FREECAD ASSEMBLY — COMPONENT RECIPES ("tinyMakeShelves")

This assembly document has 16 components, labeled P0..P15 below (a component is one placed body or linked part). 16 of them carry a construction recipe — the FreeCAD feature program that regenerates the part from scratch, quoted from this document or its linked companion documents; the rest are supplied as boundary geometry only. No exploded tour is included for this assembly.
COMPONENT P0 — recipe-attached ("expectations-Part", a linked part whose construction recipe lives in a companion FreeCAD document of the same project; that document's serialized recipe follows).
Construction recipe (the companion document, serialized — sketch geometry with constraints, then the solid features built on it; lengths are millimeters unless a unit is written):

FCSTD DOCUMENT  (FreeCAD 2023.131R26244 +5365 (Git))
Label: expectations
License: All rights reserved
LicenseURL: http://en.wikipedia.org/wiki/All_rights_reserved
objects: Sketcher::SketchObject×3, PartDesign::Pad×3, PartDesign::Body×1, App::Part×1
note: 16 computed .brp shape members not serialized (recipe doc carries the construction recipe); baked Part::Feature solids carry a one-line shape summary decoded from their .brp

FEATURE [Sketcher::SketchObject] Sketch
  ArcFitTolerance = 1e-06
  ExternalBSplineMaxDegree = 5
  ExternalBSplineTolerance = 0.0001
  FixShape = 1
  FullyConstrained = true
  InternalTolerance = 1e-06
  InvalidShape = false
  MakeInternals = false
  MapMode = 2
  TreeRank = 5
  ValidateShape = false
  sketch-geometry (6):
    g0: LineSegment StartX=0 StartY=0 StartZ=0 EndX=0 EndY=2235.2 EndZ=0
    g1: LineSegment StartX=0 StartY=2235.2 StartZ=0 EndX=685.8 EndY=2921 EndZ=0
    g2: LineSegment StartX=685.8 StartY=2921 StartZ=0 EndX=3606.8 EndY=2921 EndZ=0
    g3: LineSegment StartX=3606.8 StartY=2921 StartZ=0 EndX=4013.2 EndY=2514.6 EndZ=0
    g4: LineSegment StartX=4013.2 StartY=2514.6 StartZ=0 EndX=4013.2 EndY=0 EndZ=0
    g5: LineSegment StartX=4013.2 StartY=0 StartZ=0 EndX=0 EndY=0 EndZ=0
  constraints (17):
    c: Coincident(g0,g-1)
    c: Vertical(g0)
    c: Coincident(g1,g0)
    c: Coincident(g2,g1)
    c: Horizontal(g2)
    c: Coincident(g3,g2)
    c: Coincident(g4,g3)
    c: PointOnObject(g4,g-1)
    c: Vertical(g4)
    c: Coincident(g5,g4)
    c: Coincident(g5,g0)
    c: DistanceY(g0,g1) = 2921
    c: DistanceX(g5,g5) = 4013.2
    c: DistanceY(g0,g0) = 2235.2
    c: DistanceY(g4,g3) = 2514.6
    c: Angle(g0,g1) = 2.35619
    c: Angle(g3,g4) = 2.35619
FEATURE [PartDesign::Pad] Pad
  AddSubType = 0
  AlongSketchNormal = false
  AutoTaperInnerAngle = true
  CheckUpToFaceLimits = true
  ClaimChildren = false
  Direction = (0,0,1)
  Fit = 0
  FitJoin = 0
  FixShape = 1
  InnerFit = 0
  InnerFitJoin = 0
  InvalidShape = false
  Length = 10
  Length2 = 100
  Linearize = true
  NewSolid = false
  Profile = -> Sketch
  Reversed = true
  Suppress = false
  TaperInnerAngle = 0
  TaperInnerAngleRev = 0
  TreeRank = 16
  Type = 0
  ValidateShape = false
  _ProfileBasedVersion = 1
FEATURE [Sketcher::SketchObject] Sketch001
  ArcFitTolerance = 1e-06
  AttachmentSupport = -> [XZ_Plane]
  ExternalBSplineMaxDegree = 5
  ExternalBSplineTolerance = 0.0001
  ExternalGeometry = -> [Pad]
  FixShape = 1
  FullyConstrained = true
  InternalTolerance = 1e-06
  InvalidShape = false
  MakeInternals = false
  MapMode = 5
  Placement = pos=(0,0,0) rot=(1,0,0;1.5708rad)
  Support = -> [XZ_Plane]
  TreeRank = 17
  ValidateShape = false
  sketch-geometry (4):
    g0: LineSegment StartX=0 StartY=0 StartZ=0 EndX=4013.2 EndY=0 EndZ=0
    g1: LineSegment StartX=4013.2 StartY=0 StartZ=0 EndX=4013.2 EndY=3556 EndZ=0
    g2: LineSegment StartX=4013.2 StartY=3556 StartZ=0 EndX=0 EndY=3556 EndZ=0
    g3: LineSegment StartX=0 StartY=3556 StartZ=0 EndX=0 EndY=0 EndZ=0
  constraints (11):
    c: Coincident(g0,g1)
    c: Coincident(g1,g2)
    c: Coincident(g2,g3)
    c: Coincident(g3,g0)
    c: Horizontal(g0)
    c: Horizontal(g2)
    c: Vertical(g1)
    c: Vertical(g3)
    c: Coincident(g0,g-1)
    c: PointOnObject(g-3,g1)
    c: DistanceY(g3,g3) = 3556
FEATURE [PartDesign::Pad] Pad001
  AddSubType = 0
  AlongSketchNormal = false
  AutoTaperInnerAngle = true
  BaseFeature = -> Pad
  CheckUpToFaceLimits = true
  ClaimChildren = false
  Direction = (0,-1,-2e-16)
  Fit = 0
  FitJoin = 0
  FixShape = 1
  InnerFit = 0
  InnerFitJoin = 0
  InvalidShape = false
  Length = 10
  Length2 = 100
  Linearize = true
  NewSolid = false
  Profile = -> Sketch001
  Reversed = true
  Suppress = false
  TaperInnerAngle = 0
  TaperInnerAngleRev = 0
  TreeRank = 18
  Type = 0
  ValidateShape = false
  _ProfileBasedVersion = 1
FEATURE [Sketcher::SketchObject] Sketch002
  ArcFitTolerance = 1e-06
  AttachmentSupport = -> [Pad001]
  ExternalBSplineMaxDegree = 5
  ExternalBSplineTolerance = 0.0001
  FixShape = 1
  FullyConstrained = true
  InternalTolerance = 1e-06
  InvalidShape = false
  MakeInternals = false
  MapMode = 5
  Placement = pos=(4013.2,0,0) rot=(0.57735,0.57735,0.57735;2.0944rad)
  Support = -> [Pad001]
  TreeRank = 19
  ValidateShape = false
  sketch-geometry (5):
    g0: LineSegment StartX=0 StartY=1422.4 StartZ=0 EndX=2057.4 EndY=1422.4 EndZ=0
    g1: LineSegment StartX=2057.4 StartY=1422.4 StartZ=0 EndX=2057.4 EndY=3289.3 EndZ=0
    g2: LineSegment StartX=2057.4 StartY=3289.3 StartZ=0 EndX=0 EndY=3289.3 EndZ=0
    g3: LineSegment StartX=0 StartY=3289.3 StartZ=0 EndX=0 EndY=1422.4 EndZ=0
    g4: LineSegment [constr] StartX=0 StartY=-1.8e-15 StartZ=0 EndX=0 EndY=1422.4 EndZ=0
  constraints (14):
    c: Coincident(g0,g1)
    c: Coincident(g1,g2)
    c: Coincident(g2,g3)
    c: Coincident(g3,g0)
    c: Horizontal(g0)
    c: Horizontal(g2)
    c: Vertical(g1)
    c: Vertical(g3)
    c: Coincident(g4,g-1)
    c: Coincident(g4,g0)
    c: DistanceY(g4,g4) = 1422.4
    c: DistanceY(g3,g3) = 1866.9
    c: DistanceX(g0,g0) = 2057.4
    c: Vertical(g4)
FEATURE [PartDesign::Pad] Pad002
  AddSubType = 0
  AlongSketchNormal = false
  AutoTaperInnerAngle = true
  BaseFeature = -> Pad001
  CheckUpToFaceLimits = true
  ClaimChildren = false
  Direction = (1,0,0)
  Fit = 0
  FitJoin = 0
  FixShape = 1
  InnerFit = 0
  InnerFitJoin = 0
  InvalidShape = false
  Length = 10
  Length2 = 100
  Linearize = true
  NewSolid = false
  Profile = -> Sketch002
  Suppress = false
  TaperInnerAngle = 0
  TaperInnerAngleRev = 0
  TreeRank = 20
  Type = 0
  ValidateShape = false
  _ProfileBasedVersion = 1
FEATURE [PartDesign::Body] Body
  AutoGroupSolids = false
  ClaimAllChildren = false
  ExportMode = 0
  FixShape = 1
  Group = -> [Sketch,Pad,Sketch001,Pad001,Sketch002,Pad002]
  InvalidShape = false
  Origin = -> Origin001
  Tip = -> Pad002
  TreeRank = 15
  ValidateShape = false
  _ExportChildren = -> [Pad,Pad001,Pad002]
  _GroupVersion = 1
FEATURE [App::Part] Part  label="expectations-Part"
  ClaimAllChildren = false
  ExportMode = 1
  Group = -> [Body]
  Origin = -> Origin
  TreeRank = 4
  _ExportChildren = -> [Body]
  _GroupVersion = 1
COMPONENT P1 — recipe-attached ("Workstation-SevilleClassics_AirliftProS3-Part", a linked part whose construction recipe lives in a companion FreeCAD document of the same project; that document's serialized recipe follows).
Construction recipe (the companion document, serialized — sketch geometry with constraints, then the solid features built on it; lengths are millimeters unless a unit is written):

FCSTD DOCUMENT  (FreeCAD 2023.131R26244 +5365 (Git))
Label: Workstation-SevilleClassics_AirliftProS3
License: All rights reserved
LicenseURL: http://en.wikipedia.org/wiki/All_rights_reserved
objects: PartDesign::Pad×4, Sketcher::SketchObject×2, PartDesign::Body×1, App::Part×1
note: 17 computed .brp shape members not serialized (recipe doc carries the construction recipe); baked Part::Feature solids carry a one-line shape summary decoded from their .brp

FEATURE [Sketcher::SketchObject] Sketch
  ArcFitTolerance = 1e-06
  AttachmentSupport = -> [XY_Plane]
  ExternalBSplineMaxDegree = 5
  ExternalBSplineTolerance = 0.0001
  FixShape = 1
  FullyConstrained = true
  InternalTolerance = 1e-06
  InvalidShape = false
  MakeInternals = false
  MapMode = 5
  Support = -> [XY_Plane]
  TreeRank = 13
  ValidateShape = false
  sketch-geometry (4):
    g0: LineSegment StartX=-1479.55 StartY=0 StartZ=0 EndX=1479.55 EndY=0 EndZ=0
    g1: LineSegment StartX=1479.55 StartY=0 StartZ=0 EndX=1479.55 EndY=762 EndZ=0
    g2: LineSegment StartX=1479.55 StartY=762 StartZ=0 EndX=-1479.55 EndY=762 EndZ=0
    g3: LineSegment StartX=-1479.55 StartY=762 StartZ=0 EndX=-1479.55 EndY=0 EndZ=0
  constraints (11):
    c: Coincident(g0,g1)
    c: Coincident(g1,g2)
    c: Coincident(g2,g3)
    c: Coincident(g3,g0)
    c: Horizontal(g0)
    c: Horizontal(g2)
    c: Vertical(g1)
    c: Vertical(g3)
    c: Symmetric(g0,g0,g-1)
    c: DistanceY(g3,g3) = 762
    c: DistanceX(g0,g0) = 2959.1
FEATURE [PartDesign::Pad] Pad
  AddSubType = 0
  AlongSketchNormal = false
  AutoTaperInnerAngle = true
  CheckUpToFaceLimits = true
  ClaimChildren = false
  Direction = (0,0,1)
  Fit = 0
  FitJoin = 0
  FixShape = 1
  InnerFit = 0
  InnerFitJoin = 0
  InvalidShape = false
  Length = 76.2
  Length2 = 100
  Linearize = true
  NewSolid = false
  Profile = -> Sketch
  Reversed = true
  Suppress = false
  TaperInnerAngle = 0
  TaperInnerAngleRev = 0
  TreeRank = 14
  Type = 0
  ValidateShape = false
  _ProfileBasedVersion = 1
FEATURE [PartDesign::Pad] Pad001
  AddSubType = 0
  AlongSketchNormal = false
  AutoTaperInnerAngle = true
  CheckUpToFaceLimits = true
  ClaimChildren = false
  Direction = (0,0,1)
  Fit = 0
  FitJoin = 0
  FixShape = 1
  InnerFit = 0
  InnerFitJoin = 0
  InvalidShape = false
  Length = 965.2
  Length2 = -76.2
  Linearize = true
  NewSolid = true
  Profile = -> Sketch
  Reversed = true
  Suppress = false
  TaperInnerAngle = 0
  TaperInnerAngleRev = 0
  TreeRank = 15
  Type = 4
  ValidateShape = false
  _ProfileBasedVersion = 1
FEATURE [Sketcher::SketchObject] Sketch001
  ArcFitTolerance = 1e-06
  AttachmentSupport = -> [Sketch]
  ExternalBSplineMaxDegree = 5
  ExternalBSplineTolerance = 0.0001
  ExternalGeometry = -> [Sketch]
  FixShape = 1
  FullyConstrained = false
  InternalTolerance = 1e-06
  InvalidShape = false
  MakeInternals = false
  MapMode = 5
  Support = -> [Sketch]
  TreeRank = 16
  ValidateShape = false
  sketch-geometry (11):
    g0: LineSegment StartX=-723.9 StartY=609.6 StartZ=0 EndX=723.9 EndY=609.6 EndZ=0
    g1: LineSegment StartX=723.9 StartY=609.6 StartZ=0 EndX=1479.56 EndY=-347.179 EndZ=0
    g2: LineSegment StartX=-723.9 StartY=609.6 StartZ=0 EndX=-1479.56 EndY=-347.179 EndZ=0
    g3: LineSegment [constr] StartX=-1479.56 StartY=-347.179 StartZ=0 EndX=1479.56 EndY=-347.179 EndZ=0
    g4: GeomPoint [constr] X=1101.73 Y=131.21 Z=0
    g5: GeomPoint [constr] X=1205.36 Y=0 Z=0
    g6: LineSegment StartX=-1479.56 StartY=-347.179 StartZ=0 EndX=-1513.75 EndY=-347.179 EndZ=0
    g7: LineSegment StartX=-1513.75 StartY=-347.179 StartZ=0 EndX=-741.041 EndY=631.188 EndZ=0
    g8: LineSegment StartX=-741.041 StartY=631.188 StartZ=0 EndX=741.041 EndY=631.188 EndZ=0
    g9: LineSegment StartX=741.041 StartY=631.188 StartZ=0 EndX=1513.75 EndY=-347.179 EndZ=0
    g10: LineSegment StartX=1513.75 StartY=-347.179 StartZ=0 EndX=1479.56 EndY=-347.179 EndZ=0
  constraints (26):
    c: Symmetric(g0,g0,g-2)
    c: DistanceX(g0,g0) = 1447.8
    c: Coincident(g1,g0)
    c: Coincident(g2,g0)
    c: Coincident(g3,g2)
    c: Coincident(g3,g1)
    c: Symmetric(g1,g2,g-2)
    c: Distance(g1) = 1219.2
    c: DistanceY(g0,g-3) = 152.4
    c: Symmetric(g1,g1,g4)
    c: PointOnObject(g5,g1)
    c: PointOnObject(g5,g-1)
    c: Distance(g5,g4) = 167.198
    c: DistanceX(g2,g-3) = 0.01
    c: Coincident(g6,g2)
    c: PointOnObject(g6,g3)
    c: Coincident(g7,g6)
    c: Coincident(g8,g7)
    c: Horizontal(g8)
    c: Coincident(g9,g8)
    c: PointOnObject(g9,g3)
    c: Coincident(g10,g9)
    c: Coincident(g10,g1)
    c: Equal(g6,g10)
    c: Equal(g7,g9)
    c: Parallel(g9,g1)
FEATURE [PartDesign::Pad] Pad002
  AddSubType = 0
  AlongSketchNormal = false
  AutoTaperInnerAngle = true
  CheckUpToFaceLimits = true
  ClaimChildren = false
  Direction = (0,0,1)
  Fit = 0
  FitJoin = 0
  FixShape = 1
  InnerFit = 0
  InnerFitJoin = 0
  InvalidShape = false
  Length = 965.2
  Length2 = 100
  Linearize = true
  NewSolid = true
  Profile = -> Sketch001
  Suppress = false
  TaperInnerAngle = 0
  TaperInnerAngleRev = 0
  TreeRank = 17
  Type = 0
  ValidateShape = false
  _ProfileBasedVersion = 1
FEATURE [PartDesign::Pad] Pad003
  AddSubType = 0
  AlongSketchNormal = false
  AutoTaperInnerAngle = true
  CheckUpToFaceLimits = true
  ClaimChildren = false
  Direction = (0,0,1)
  Fit = 0
  FitJoin = 0
  FixShape = 1
  InnerFit = 0
  InnerFitJoin = 0
  InvalidShape = false
  Length = 609.6
  Length2 = -76.2
  Linearize = true
  NewSolid = true
  Profile = -> Sketch
  Reversed = true
  Suppress = false
  TaperInnerAngle = 0
  TaperInnerAngleRev = 0
  TreeRank = 18
  Type = 4
  ValidateShape = false
  _ProfileBasedVersion = 1
FEATURE [PartDesign::Body] Body
  AutoGroupSolids = false
  ClaimAllChildren = false
  ExportMode = 0
  FixShape = 1
  Group = -> [Sketch,Pad,Pad001,Sketch001,Pad002,Pad003]
  InvalidShape = false
  Origin = -> Origin001
  Tip = -> Pad003
  TreeRank = 12
  ValidateShape = false
  _ExportChildren = -> [Pad,Pad001,Pad002,Pad003]
  _GroupVersion = 1
FEATURE [App::Part] Part  label="Workstation-SevilleClassics_AirliftProS3-Part"
  ClaimAllChildren = false
  ExportMode = 1
  Group = -> [Body]
  Origin = -> Origin
  TreeRank = 1
  _ExportChildren = -> [Body]
  _GroupVersion = 1
COMPONENT P2 — recipe-attached ("roadLegalWidth-Body", a linked part whose construction recipe lives in a companion FreeCAD document of the same project; that document's serialized recipe follows).
Construction recipe (the companion document, serialized — sketch geometry with constraints, then the solid features built on it; lengths are millimeters unless a unit is written):

FCSTD DOCUMENT  (FreeCAD 2023.131R26244 +5365 (Git))
Label: roadLegalWidth
License: All rights reserved
LicenseURL: http://en.wikipedia.org/wiki/All_rights_reserved
objects: Sketcher::SketchObject×1, PartDesign::Pad×1, PartDesign::Body×1, App::Part×1
note: 6 computed .brp shape members not serialized (recipe doc carries the construction recipe); baked Part::Feature solids carry a one-line shape summary decoded from their .brp

FEATURE [Sketcher::SketchObject] Sketch
  ArcFitTolerance = 1e-06
  AttachmentSupport = -> [XY_Plane]
  ExternalBSplineMaxDegree = 5
  ExternalBSplineTolerance = 0.0001
  FullyConstrained = true
  InternalTolerance = 1e-06
  InvalidShape = false
  MakeInternals = false
  MapMode = 5
  Support = -> [XY_Plane]
  TreeRank = 10
  ValidateShape = true
  sketch-geometry (4):
    g0: LineSegment StartX=0 StartY=0 StartZ=0 EndX=2590.8 EndY=0 EndZ=0
    g1: LineSegment StartX=2590.8 StartY=0 StartZ=0 EndX=2590.8 EndY=12192 EndZ=0
    g2: LineSegment StartX=2590.8 StartY=12192 StartZ=0 EndX=0 EndY=12192 EndZ=0
    g3: LineSegment StartX=0 StartY=12192 StartZ=0 EndX=0 EndY=0 EndZ=0
  constraints (11):
    c: Coincident(g0,g1)
    c: Coincident(g1,g2)
    c: Coincident(g2,g3)
    c: Coincident(g3,g0)
    c: Horizontal(g0)
    c: Horizontal(g2)
    c: Vertical(g1)
    c: Vertical(g3)
    c: Coincident(g0,g-1)
    c: DistanceX(g0,g0) = 2590.8
    c: DistanceY(g3,g3) = 12192
FEATURE [PartDesign::Pad] Pad
  AddSubType = 0
  AlongSketchNormal = false
  AutoTaperInnerAngle = true
  CheckUpToFaceLimits = true
  ClaimChildren = false
  Direction = (0,0,1)
  Fit = 0
  FitJoin = 0
  FixShape = 1
  InnerFit = 0
  InnerFitJoin = 0
  InvalidShape = false
  Length = 10
  Length2 = 100
  Linearize = true
  NewSolid = false
  Profile = -> Sketch
  Reversed = true
  Suppress = false
  TaperInnerAngle = 0
  TaperInnerAngleRev = 0
  TreeRank = 11
  Type = 0
  ValidateShape = false
  _ProfileBasedVersion = 1
FEATURE [PartDesign::Body] Body  label="roadLegalWidth-Body"
  AutoGroupSolids = false
  ClaimAllChildren = false
  ExportMode = 0
  Group = -> [Sketch,Pad]
  InvalidShape = false
  Origin = -> Origin
  Tip = -> Pad
  TreeRank = 9
  ValidateShape = true
  _ExportChildren = -> [Pad]
  _GroupVersion = 1
FEATURE [App::Part] Part  label="roadLegalWidth-Part"
  ClaimAllChildren = false
  ExportMode = 1
  Group = -> [Body]
  Origin = -> Origin001
  TreeRank = 14
  _ExportChildren = -> [Body]
  _GroupVersion = 1
COMPONENT P3 — recipe-attached ("bedQueen-Part", a linked part whose construction recipe lives in a companion FreeCAD document of the same project; that document's serialized recipe follows).
Construction recipe (the companion document, serialized — sketch geometry with constraints, then the solid features built on it; lengths are millimeters unless a unit is written):

FCSTD DOCUMENT  (FreeCAD 2023.131R26244 +5365 (Git))
Label: bedQueen
License: All rights reserved
LicenseURL: http://en.wikipedia.org/wiki/All_rights_reserved
objects: PartDesign::Pad×2, Sketcher::SketchObject×1, PartDesign::Body×1, App::Part×1
note: 9 computed .brp shape members not serialized (recipe doc carries the construction recipe); baked Part::Feature solids carry a one-line shape summary decoded from their .brp

FEATURE [Sketcher::SketchObject] Sketch
  ArcFitTolerance = 1e-06
  AttachmentSupport = -> [XY_Plane]
  ExternalBSplineMaxDegree = 5
  ExternalBSplineTolerance = 0.0001
  FixShape = 1
  FullyConstrained = true
  InternalTolerance = 1e-06
  InvalidShape = false
  MakeInternals = false
  MapMode = 5
  Support = -> [XY_Plane]
  TreeRank = 10
  ValidateShape = false
  sketch-geometry (4):
    g0: LineSegment StartX=0 StartY=0 StartZ=0 EndX=1524 EndY=0 EndZ=0
    g1: LineSegment StartX=1524 StartY=0 StartZ=0 EndX=1524 EndY=2032 EndZ=0
    g2: LineSegment StartX=1524 StartY=2032 StartZ=0 EndX=0 EndY=2032 EndZ=0
    g3: LineSegment StartX=0 StartY=2032 StartZ=0 EndX=0 EndY=0 EndZ=0
  constraints (11):
    c: Coincident(g0,g1)
    c: Coincident(g1,g2)
    c: Coincident(g2,g3)
    c: Coincident(g3,g0)
    c: Horizontal(g0)
    c: Horizontal(g2)
    c: Vertical(g1)
    c: Vertical(g3)
    c: Coincident(g0,g-1)
    c: DistanceX(g0,g0) = 1524
    c: DistanceY(g3,g3) = 2032
FEATURE [PartDesign::Pad] Pad
  AddSubType = 0
  AlongSketchNormal = false
  AutoTaperInnerAngle = true
  CheckUpToFaceLimits = true
  ClaimChildren = false
  Direction = (0,0,1)
  Fit = 0
  FitJoin = 0
  FixShape = 1
  InnerFit = 0
  InnerFitJoin = 0
  InvalidShape = false
  Length = 215.9
  Length2 = 100
  Linearize = true
  NewSolid = false
  Profile = -> Sketch
  Reversed = true
  Suppress = false
  TaperInnerAngle = 0
  TaperInnerAngleRev = 0
  TreeRank = 11
  Type = 0
  ValidateShape = false
  _ProfileBasedVersion = 1
FEATURE [PartDesign::Pad] Pad001
  AddSubType = 0
  AlongSketchNormal = false
  AutoTaperInnerAngle = true
  CheckUpToFaceLimits = true
  ClaimChildren = false
  Direction = (0,0,1)
  Fit = 0
  FitJoin = 0
  FixShape = 1
  InnerFit = 0
  InnerFitJoin = 0
  InvalidShape = false
  Length = 812.8
  Length2 = 100
  Linearize = true
  NewSolid = true
  Profile = -> Sketch
  Suppress = false
  TaperInnerAngle = 0
  TaperInnerAngleRev = 0
  TreeRank = 12
  Type = 0
  ValidateShape = false
  _ProfileBasedVersion = 1
FEATURE [PartDesign::Body] Body  label="bedQueen-Body"
  AutoGroupSolids = false
  ClaimAllChildren = false
  ExportMode = 0
  FixShape = 1
  Group = -> [Sketch,Pad,Pad001]
  InvalidShape = false
  Origin = -> Origin
  Tip = -> Pad001
  TreeRank = 9
  ValidateShape = false
  _ExportChildren = -> [Pad,Pad001]
  _GroupVersion = 1
FEATURE [App::Part] Part  label="bedQueen-Part"
  ClaimAllChildren = false
  ExportMode = 1
  Group = -> [Body]
  Origin = -> Origin001
  TreeRank = 15
  _ExportChildren = -> [Body]
  _GroupVersion = 1
COMPONENT P4 — recipe-attached ("human-Part", a linked part whose construction recipe lives in a companion FreeCAD document of the same project; that document's serialized recipe follows).
Construction recipe (the companion document, serialized — sketch geometry with constraints, then the solid features built on it; lengths are millimeters unless a unit is written):

FCSTD DOCUMENT  (FreeCAD 2023.131R26244 +5365 (Git))
Label: human
License: All rights reserved
LicenseURL: http://en.wikipedia.org/wiki/All_rights_reserved
objects: Sketcher::SketchObject×1, PartDesign::Pad×1, PartDesign::Body×1, App::Part×1
note: 6 computed .brp shape members not serialized (recipe doc carries the construction recipe); baked Part::Feature solids carry a one-line shape summary decoded from their .brp

FEATURE [Sketcher::SketchObject] Sketch
  ArcFitTolerance = 1e-06
  AttachmentSupport = -> [XY_Plane]
  ExternalBSplineMaxDegree = 5
  ExternalBSplineTolerance = 0.0001
  FixShape = 1
  FullyConstrained = true
  InternalTolerance = 1e-06
  InvalidShape = false
  MakeInternals = false
  MapMode = 5
  Support = -> [XY_Plane]
  TreeRank = 13
  ValidateShape = false
  sketch-geometry (4):
    g0: LineSegment StartX=0 StartY=0 StartZ=0 EndX=609.6 EndY=0 EndZ=0
    g1: LineSegment StartX=609.6 StartY=0 StartZ=0 EndX=609.6 EndY=609.6 EndZ=0
    g2: LineSegment StartX=609.6 StartY=609.6 StartZ=0 EndX=0 EndY=609.6 EndZ=0
    g3: LineSegment StartX=0 StartY=609.6 StartZ=0 EndX=0 EndY=0 EndZ=0
  constraints (11):
    c: Coincident(g0,g1)
    c: Coincident(g1,g2)
    c: Coincident(g2,g3)
    c: Coincident(g3,g0)
    c: Horizontal(g0)
    c: Horizontal(g2)
    c: Vertical(g1)
    c: Vertical(g3)
    c: Coincident(g0,g-1)
    c: DistanceX(g0,g0) = 609.6
    c: DistanceY(g3,g3) = 609.6
FEATURE [PartDesign::Pad] Pad
  AddSubType = 0
  AlongSketchNormal = false
  AutoTaperInnerAngle = true
  CheckUpToFaceLimits = true
  ClaimChildren = false
  Direction = (0,0,1)
  Fit = 0
  FitJoin = 0
  FixShape = 1
  InnerFit = 0
  InnerFitJoin = 0
  InvalidShape = false
  Length = 1727.2
  Length2 = 100
  Linearize = true
  NewSolid = false
  Profile = -> Sketch
  Suppress = false
  TaperInnerAngle = 0
  TaperInnerAngleRev = 0
  TreeRank = 14
  Type = 0
  ValidateShape = false
  _ProfileBasedVersion = 1
FEATURE [PartDesign::Body] Body
  AutoGroupSolids = false
  ClaimAllChildren = false
  ExportMode = 0
  FixShape = 1
  Group = -> [Sketch,Pad]
  InvalidShape = false
  Origin = -> Origin001
  Tip = -> Pad
  TreeRank = 12
  ValidateShape = false
  _ExportChildren = -> [Pad]
  _GroupVersion = 1
FEATURE [App::Part] Part  label="human-Part"
  ClaimAllChildren = false
  ExportMode = 1
  Group = -> [Body]
  Origin = -> Origin
  TreeRank = 1
  _ExportChildren = -> [Body]
  _GroupVersion = 1
COMPONENT P5 — recipe-attached ("verticalTimber-Part", a linked part whose construction recipe lives in a companion FreeCAD document of the same project; that document's serialized recipe follows).
Construction recipe (the companion document, serialized — sketch geometry with constraints, then the solid features built on it; lengths are millimeters unless a unit is written):

FCSTD DOCUMENT  (FreeCAD 2023.131R26244 +5365 (Git))
Label: verticalTimber
License: All rights reserved
LicenseURL: http://en.wikipedia.org/wiki/All_rights_reserved
objects: Sketcher::SketchObject×1, PartDesign::Pad×1, PartDesign::Body×1, App::Part×1
note: 6 computed .brp shape members not serialized (recipe doc carries the construction recipe); baked Part::Feature solids carry a one-line shape summary decoded from their .brp

FEATURE [Sketcher::SketchObject] Sketch
  ArcFitTolerance = 1e-06
  AttachmentSupport = -> [XY_Plane]
  ExternalBSplineMaxDegree = 5
  ExternalBSplineTolerance = 0.0001
  FixShape = 1
  FullyConstrained = true
  InternalTolerance = 1e-06
  InvalidShape = false
  MakeInternals = false
  MapMode = 5
  Support = -> [XY_Plane]
  TreeRank = 13
  ValidateShape = false
  sketch-geometry (4):
    g0: LineSegment StartX=0 StartY=0 StartZ=0 EndX=88.9 EndY=0 EndZ=0
    g1: LineSegment StartX=88.9 StartY=0 StartZ=0 EndX=88.9 EndY=38.1 EndZ=0
    g2: LineSegment StartX=88.9 StartY=38.1 StartZ=0 EndX=0 EndY=38.1 EndZ=0
    g3: LineSegment StartX=0 StartY=38.1 StartZ=0 EndX=0 EndY=0 EndZ=0
  constraints (11):
    c: Coincident(g0,g1)
    c: Coincident(g1,g2)
    c: Coincident(g2,g3)
    c: Coincident(g3,g0)
    c: Horizontal(g0)
    c: Horizontal(g2)
    c: Vertical(g1)
    c: Vertical(g3)
    c: Coincident(g0,g-1)
    c: DistanceX(g0,g0) = 88.9
    c: DistanceY(g3,g3) = 38.1
FEATURE [PartDesign::Pad] Pad
  AddSubType = 0
  AlongSketchNormal = false
  AutoTaperInnerAngle = true
  CheckUpToFaceLimits = true
  ClaimChildren = false
  Direction = (0,0,1)
  Fit = 0
  FitJoin = 0
  FixShape = 1
  InnerFit = 0
  InnerFitJoin = 0
  InvalidShape = false
  Length = 2171.7
  Length2 = 100
  Linearize = true
  NewSolid = false
  Profile = -> Sketch
  Suppress = false
  TaperInnerAngle = 0
  TaperInnerAngleRev = 0
  TreeRank = 14
  Type = 0
  ValidateShape = false
  _ProfileBasedVersion = 1
FEATURE [PartDesign::Body] Body
  AutoGroupSolids = false
  ClaimAllChildren = false
  ExportMode = 0
  FixShape = 1
  Group = -> [Sketch,Pad]
  InvalidShape = false
  Origin = -> Origin001
  Tip = -> Pad
  TreeRank = 12
  ValidateShape = false
  _ExportChildren = -> [Pad]
  _GroupVersion = 1
FEATURE [App::Part] Part  label="verticalTimber-Part"
  ClaimAllChildren = false
  ExportMode = 1
  Group = -> [Body]
  Origin = -> Origin
  TreeRank = 1
  _ExportChildren = -> [Body]
  _GroupVersion = 1
COMPONENT P6 — same part as P5; its construction recipe is shown at P5.
COMPONENT P7 — same part as P5; its construction recipe is shown at P5.
COMPONENT P8 — same part as P5; its construction recipe is shown at P5.
COMPONENT P9 — same part as P5; its construction recipe is shown at P5.
COMPONENT P10 — same part as P5; its construction recipe is shown at P5.
COMPONENT P11 — same part as P5; its construction recipe is shown at P5.
COMPONENT P12 — same part as P5; its construction recipe is shown at P5.
COMPONENT P13 — same part as P5; its construction recipe is shown at P5.
COMPONENT P14 — same part as P5; its construction recipe is shown at P5.
COMPONENT P15 — recipe-attached ("workbench-Part", a linked part whose construction recipe lives in a companion FreeCAD document of the same project; that document's serialized recipe follows).
Construction recipe (the companion document, serialized — sketch geometry with constraints, then the solid features built on it; lengths are millimeters unless a unit is written):

FCSTD DOCUMENT  (FreeCAD 2023.131R26244 +5365 (Git))
Label: workbench
License: All rights reserved
LicenseURL: http://en.wikipedia.org/wiki/All_rights_reserved
objects: PartDesign::Pad×2, Sketcher::SketchObject×1, PartDesign::Body×1, App::Part×1
note: 9 computed .brp shape members not serialized (recipe doc carries the construction recipe); baked Part::Feature solids carry a one-line shape summary decoded from their .brp

FEATURE [Sketcher::SketchObject] Sketch
  ArcFitTolerance = 1e-06
  AttachmentSupport = -> [XY_Plane]
  ExternalBSplineMaxDegree = 5
  ExternalBSplineTolerance = 0.0001
  FixShape = 1
  FullyConstrained = true
  InternalTolerance = 1e-06
  InvalidShape = false
  MakeInternals = false
  MapMode = 5
  Support = -> [XY_Plane]
  TreeRank = 13
  ValidateShape = false
  sketch-geometry (4):
    g0: LineSegment StartX=0 StartY=0 StartZ=0 EndX=1219.2 EndY=0 EndZ=0
    g1: LineSegment StartX=1219.2 StartY=0 StartZ=0 EndX=1219.2 EndY=609.6 EndZ=0
    g2: LineSegment StartX=1219.2 StartY=609.6 StartZ=0 EndX=0 EndY=609.6 EndZ=0
    g3: LineSegment StartX=0 StartY=609.6 StartZ=0 EndX=0 EndY=0 EndZ=0
  constraints (11):
    c: Coincident(g0,g1)
    c: Coincident(g1,g2)
    c: Coincident(g2,g3)
    c: Coincident(g3,g0)
    c: Horizontal(g0)
    c: Horizontal(g2)
    c: Vertical(g1)
    c: Vertical(g3)
    c: Coincident(g0,g-1)
    c: DistanceX(g0,g0) = 1219.2
    c: DistanceY(g3,g3) = 609.6
FEATURE [PartDesign::Pad] Pad
  AddSubType = 0
  AlongSketchNormal = false
  AutoTaperInnerAngle = true
  CheckUpToFaceLimits = true
  ClaimChildren = false
  Direction = (0,0,1)
  Fit = 0
  FitJoin = 0
  FixShape = 1
  InnerFit = 0
  InnerFitJoin = 0
  InvalidShape = false
  Length = 63.5
  Length2 = 100
  Linearize = true
  NewSolid = false
  Profile = -> Sketch
  Suppress = false
  TaperInnerAngle = 0
  TaperInnerAngleRev = 0
  TreeRank = 14
  Type = 0
  ValidateShape = false
  _ProfileBasedVersion = 1
FEATURE [PartDesign::Pad] Pad001
  AddSubType = 0
  AlongSketchNormal = false
  AutoTaperInnerAngle = true
  BaseFeature = -> Pad
  CheckUpToFaceLimits = true
  ClaimChildren = false
  Direction = (0,0,1)
  Fit = 0
  FitJoin = 0
  FixShape = 1
  InnerFit = 0
  InnerFitJoin = 0
  InvalidShape = false
  Length = 546.1
  Length2 = 100
  Linearize = true
  NewSolid = false
  Profile = -> Sketch
  Reversed = true
  Suppress = false
  TaperInnerAngle = 0
  TaperInnerAngleRev = 0
  TreeRank = 15
  Type = 0
  ValidateShape = false
  _ProfileBasedVersion = 1
FEATURE [PartDesign::Body] Body
  AutoGroupSolids = false
  ClaimAllChildren = false
  ExportMode = 0
  FixShape = 1
  Group = -> [Sketch,Pad,Pad001]
  InvalidShape = false
  Origin = -> Origin001
  Tip = -> Pad001
  TreeRank = 12
  ValidateShape = false
  _ExportChildren = -> [Pad,Pad001]
  _GroupVersion = 1
FEATURE [App::Part] Part  label="workbench-Part"
  ClaimAllChildren = false
  ExportMode = 1
  Group = -> [Body]
  Origin = -> Origin
  TreeRank = 1
  _ExportChildren = -> [Body]
  _GroupVersion = 1
PROVENANCE & LICENSES
A FreeCAD (.FCStd) document from a public repository crawl; recipes are the document's own serialized feature recipes (and, for linked parts, companion documents' recipes).
License: agpl-3.0.
